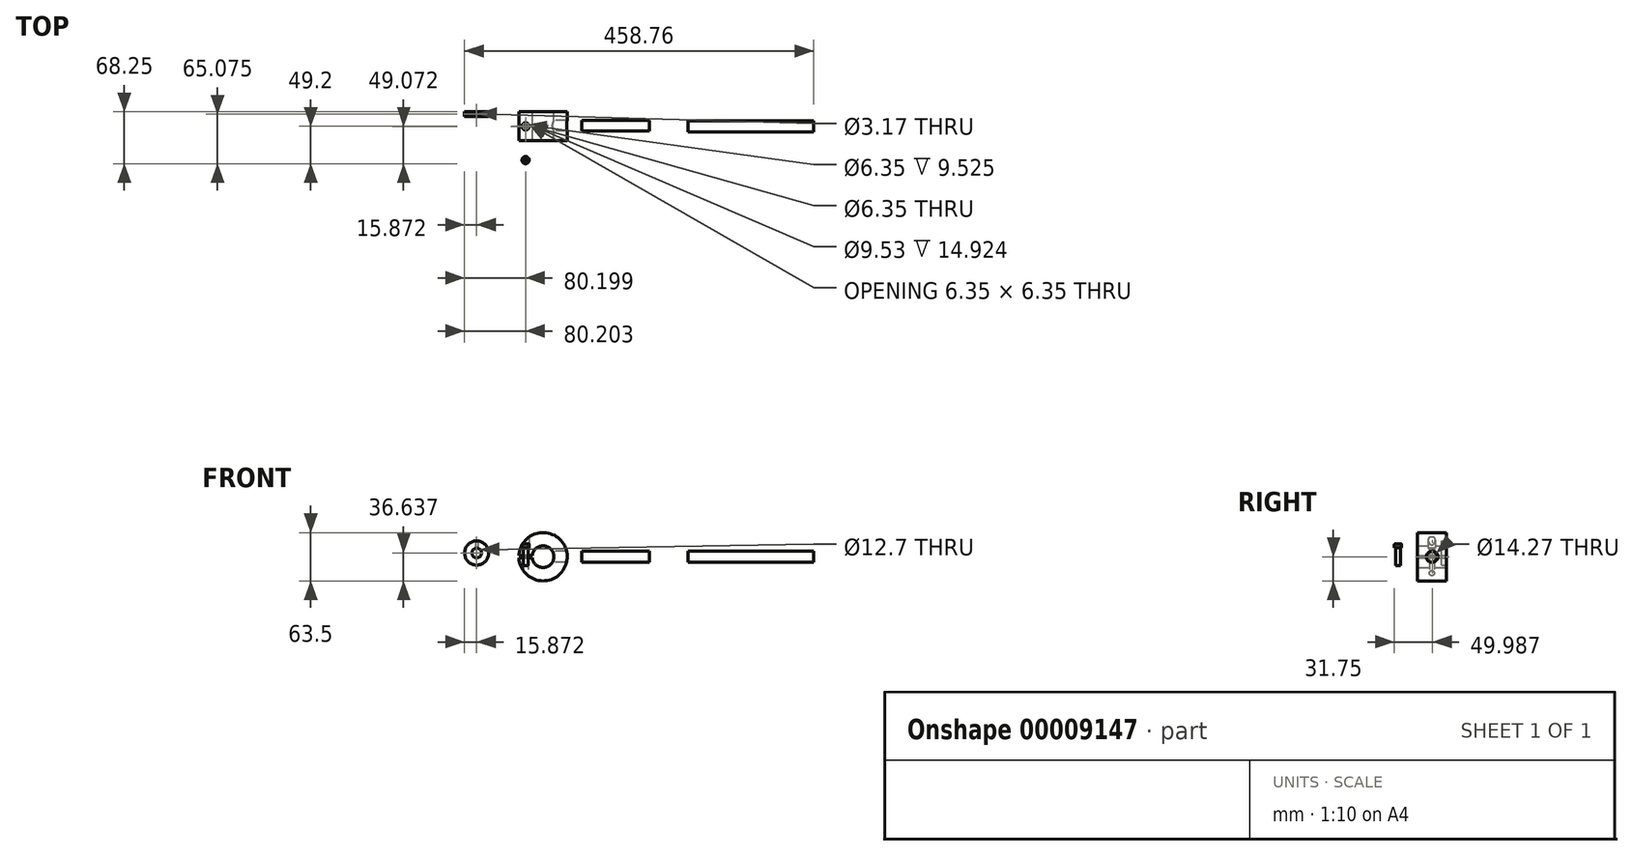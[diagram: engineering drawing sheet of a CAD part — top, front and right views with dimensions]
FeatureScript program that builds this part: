
annotation { "Feature Type Name" : "Feature", "Feature Type Description" : "" }
export const myFeature = defineFeature(function(context is Context, id is Id, definition is map)
    precondition{}
    {
        {
            var Q0;
            Q0=qCreatedBy(makeId("Front.planeOp"),FACE);
            var sketch = newSketch(context, id + "F0", { "sketchPlane" : qUnion([Q0])});
            skCircle(sketch, "E0", {"center": v(0, 0) * mm, "radius": 14.29 * mm});
            skCircle(sketch, "E1", {"center": v(0, 0) * mm, "radius": 31.75 * mm});
            skLineSegment(sketch, "E2", {"start": v(-31.71, 1.57) * mm, "end": v(-10.18, 1.57) * mm});
            skLineSegment(sketch, "E3", {"start": v(-31.71, -1.57) * mm, "end": v(-9.23, -1.57) * mm});
            skSolve(sketch);
        }
        {
            var Q0;
            {var subQ1=sQuery(id+"F0.wireOp",EDGE,"E0");var subQ5=sQuery(id+"F0.wireOp",EDGE,"E2");var subQ6=makeQuery(id+"F0.imprint","INTERSECT",VERTEX,{"derivedFrom":[subQ1,subQ5]});Q0=makeQuery(id+"F0.imprint","IMPRINT",FACE,{"disambiguationData":[TD([[makeQuery(id+"F0.imprint","IMPRINT",EDGE,{"disambiguationData":[TD([[subQ6,1.0]])],"derivedFrom":subQ1}),-1.0]])]});}
            extrude(context, id + "F1", {"entities" : qUnion([Q0]), "depth" : 38.1 * mm});
        }
        {
            var Q0;
            Q0=qCreatedBy(makeId("Right.planeOp"),FACE);
            cPlane(context, id + "F2", {"entities" : qUnion([Q0]), "cplaneType" : CPlaneType.OFFSET, "offset" : 50.8 * mm, "width" : 152.4 * mm, "height" : 152.4 * mm});
        }
        {
            var Q0;
            Q0=qCreatedBy(makeId("Right.planeOp"),FACE);
            var sketch = newSketch(context, id + "F3", { "sketchPlane" : qUnion([Q0])});
            skCircle(sketch, "E4", {"center": v(-18.26, 0) * mm, "radius": 7.14 * mm});
            skSolve(sketch);
        }
        {
            var Q0;
            Q0=makeQuery(id+"F3.imprint","IMPRINT",FACE,{"disambiguationData":[TD([[makeQuery(id+"F3.imprint","IMPRINT",EDGE,{"derivedFrom":sQuery(id+"F3.wireOp",EDGE,"E4")}),1.0]])]});
            extrude(context, id + "F4", {"entities" : qUnion([Q0]), "operationType" : NewBodyOperationType.REMOVE, "endBound" : BoundingType.THROUGH_ALL, "depth" : 25.4 * mm});
        }
        {
            var Q0;
            Q0=qCreatedBy(id+"F2.planeOp",FACE);
            var sketch = newSketch(context, id + "F5", { "sketchPlane" : qUnion([Q0])});
            skCircle(sketch, "E5", {"center": v(-18.26, 0) * mm, "radius": 7.14 * mm});
            skSolve(sketch);
        }
        {
            var Q0;
            Q0=makeQuery(id+"F5.imprint","IMPRINT",FACE,{"disambiguationData":[TD([[makeQuery(id+"F5.imprint","IMPRINT",EDGE,{"derivedFrom":sQuery(id+"F5.wireOp",EDGE,"E5")}),1.0]])]});
            extrude(context, id + "F6", {"entities" : qUnion([Q0]), "depth" : 88.9 * mm});
        }
        {
            var Q0;
            Q0=makeQuery(id+"F1.opExtrude","SWEPT_FACE",FACE,{"disambiguationData":[OSD([sQuery(id+"F0.wireOp",EDGE,"E3")])]});
            var sketch = newSketch(context, id + "F7", { "sketchPlane" : qUnion([Q0])});
            skLineSegment(sketch, "E6.bottom", {"start": v(-31.71, 0) * mm, "end": v(-14.25, 0) * mm});
            skLineSegment(sketch, "E6.top", {"start": v(-31.71, -38.1) * mm, "end": v(-14.25, -38.1) * mm});
            skLineSegment(sketch, "E6.left", {"start": v(-31.71, 0) * mm, "end": v(-31.71, -38.1) * mm});
            skLineSegment(sketch, "E6.right", {"start": v(-14.25, 0) * mm, "end": v(-14.25, -38.1) * mm});
            skCircle(sketch, "E7", {"center": v(-22.96, -19.05) * mm, "radius": 3.18 * mm});
            skSolve(sketch);
        }
        {
            var Q0;
            Q0=makeQuery(id+"F7.imprint","IMPRINT",FACE,{"disambiguationData":[TD([[makeQuery(id+"F7.imprint","IMPRINT",EDGE,{"derivedFrom":sQuery(id+"F7.wireOp",EDGE,"E7")}),1.0]])]});
            extrude(context, id + "F8", {"entities" : qUnion([Q0]), "operationType" : NewBodyOperationType.REMOVE, "endBound" : BoundingType.THROUGH_ALL, "depth" : 25.4 * mm, "hasSecondDirection" : true, "secondDirectionBound" : SecondDirectionBoundingType.THROUGH_ALL, "secondDirectionOppositeDirection" : true, "secondDirectionDepth" : 25.4 * mm});
        }
        {
            var Q0;
            Q0=makeQuery(id+"F1.opExtrude","SWEPT_FACE",FACE,{"disambiguationData":[OSD([sQuery(id+"F0.wireOp",EDGE,"E2")])]});
            cPlane(context, id + "F9", {"entities" : qUnion([Q0]), "cplaneType" : CPlaneType.OFFSET, "offset" : 12.7 * mm, "oppositeDirection" : true, "width" : 152.4 * mm, "height" : 152.4 * mm});
        }
        {
            var Q0;
            Q0=qCreatedBy(id+"F9.planeOp",FACE);
            var sketch = newSketch(context, id + "F10", { "sketchPlane" : qUnion([Q0])});
            skCircle(sketch, "E8", {"center": v(-22.96, 19.18) * mm, "radius": 4.76 * mm});
            skSolve(sketch);
        }
        {
            var Q0;
            Q0=makeQuery(id+"F10.imprint","IMPRINT",FACE,{"disambiguationData":[TD([[makeQuery(id+"F10.imprint","IMPRINT",EDGE,{"derivedFrom":sQuery(id+"F10.wireOp",EDGE,"E8")}),1.0]])]});
            extrude(context, id + "F11", {"entities" : qUnion([Q0]), "operationType" : NewBodyOperationType.REMOVE, "endBound" : BoundingType.THROUGH_ALL, "oppositeDirection" : true, "depth" : 25.4 * mm, "hasSecondDirection" : true, "secondDirectionOppositeDirection" : false, "secondDirectionDepth" : 3.17 * mm});
        }
        {
            var Q0;
            Q0=makeQuery(id+"F6.opExtrude","CAP_FACE",FACE,{"disambiguationData":[OSD([sQuery(id+"F5.wireOp",EDGE,"E5")])],"isStart":false});
            cPlane(context, id + "F12", {"entities" : qUnion([Q0]), "cplaneType" : CPlaneType.OFFSET, "offset" : 50.8 * mm, "width" : 152.4 * mm, "height" : 152.4 * mm});
        }
        {
            var Q0;
            Q0=qCreatedBy(id+"F12.planeOp",FACE);
            var sketch = newSketch(context, id + "F13", { "sketchPlane" : qUnion([Q0])});
            skCircle(sketch, "E9", {"center": v(-19.18, -0.1) * mm, "radius": 7.14 * mm});
            skSolve(sketch);
        }
        {
            var Q0;
            Q0=makeQuery(id+"F13.imprint","IMPRINT",FACE,{"disambiguationData":[TD([[makeQuery(id+"F13.imprint","IMPRINT",EDGE,{"derivedFrom":sQuery(id+"F13.wireOp",EDGE,"E9")}),1.0]])]});
            extrude(context, id + "F14", {"entities" : qUnion([Q0]), "depth" : 165.1 * mm});
        }
        {
            var Q0;
            Q0=makeQuery(id+"F1.opExtrude","CAP_FACE",FACE,{"disambiguationData":[OSD([sQuery(id+"F0.wireOp",EDGE,"E0"),sQuery(id+"F0.wireOp",EDGE,"E1"),sQuery(id+"F0.wireOp",EDGE,"E2"),sQuery(id+"F0.wireOp",EDGE,"E3")])],"isStart":false});
            cPlane(context, id + "F15", {"entities" : qUnion([Q0]), "cplaneType" : CPlaneType.OFFSET, "offset" : 25.4 * mm, "width" : 152.4 * mm, "height" : 152.4 * mm});
        }
        {
            var Q0;
            Q0=qCreatedBy(id+"F15.planeOp",FACE);
            var sketch = newSketch(context, id + "F16", { "sketchPlane" : qUnion([Q0])});
            skLineSegment(sketch, "E10", {"start": v(-23, 16.6) * mm, "end": v(-18.25, 16.6) * mm});
            skLineSegment(sketch, "E11", {"start": v(-18.25, 16.6) * mm, "end": v(-18.25, 11.84) * mm});
            skLineSegment(sketch, "E12", {"start": v(-18.25, 11.84) * mm, "end": v(-19.83, 11.84) * mm});
            skLineSegment(sketch, "E13", {"start": v(-19.83, 11.84) * mm, "end": v(-19.83, -11.98) * mm});
            skLineSegment(sketch, "E14", {"start": v(-19.83, -11.98) * mm, "end": v(-23, -11.98) * mm});
            skLineSegment(sketch, "E15", {"start": v(-23, -11.98) * mm, "end": v(-23, 16.6) * mm});
            skSolve(sketch);
        }
        {
            var Q0;
            Q0=makeQuery(id+"F16.imprint","IMPRINT",FACE,{"disambiguationData":[TD([[makeQuery(id+"F16.imprint","IMPRINT",EDGE,{"derivedFrom":sQuery(id+"F16.wireOp",EDGE,"E10")}),-1.0]])]});
            var Q1;
            Q1=sQuery(id+"F16.wireOp",EDGE,"E15");
            revolve(context, id + "F17", {"entities" : qUnion([Q0]), "axis" : qUnion([Q1]), "revolveType" : RevolveType.FULL});
        }
        {
            var Q0;
            Q0=makeQuery(id+"F17.opRevolve","SWEPT_FACE",FACE,{"disambiguationData":[OSD([sQuery(id+"F16.wireOp",EDGE,"E10")])]});
            var sketch = newSketch(context, id + "F18", { "sketchPlane" : qUnion([Q0])});
            skCircle(sketch, "E16.cCircle", {"center": v(-23, -63.5) * mm, "radius": 2.37 * mm, "construction": true});
            skLineSegment(sketch, "E16.0", {"start": v(-24.37, -61.13) * mm, "end": v(-21.63, -61.13) * mm});
            skLineSegment(sketch, "E16.1", {"start": v(-21.63, -61.13) * mm, "end": v(-20.26, -63.5) * mm});
            skLineSegment(sketch, "E16.2", {"start": v(-20.26, -63.5) * mm, "end": v(-21.63, -65.87) * mm});
            skLineSegment(sketch, "E16.3", {"start": v(-21.63, -65.87) * mm, "end": v(-24.37, -65.87) * mm});
            skLineSegment(sketch, "E16.4", {"start": v(-24.37, -65.87) * mm, "end": v(-25.75, -63.5) * mm});
            skLineSegment(sketch, "E16.5", {"start": v(-25.75, -63.5) * mm, "end": v(-24.37, -61.13) * mm});
            skPoint(sketch, "E16.0.midPoint", {"position": v(-23, -61.13) * mm});
            skSolve(sketch);
        }
        {
            var Q0;
            Q0=makeQuery(id+"F18.imprint","IMPRINT",FACE,{"disambiguationData":[TD([[makeQuery(id+"F18.imprint","IMPRINT",EDGE,{"derivedFrom":sQuery(id+"F18.wireOp",EDGE,"E16.0")}),-1.0]])]});
            extrude(context, id + "F19", {"entities" : qUnion([Q0]), "operationType" : NewBodyOperationType.REMOVE, "oppositeDirection" : true, "depth" : 4.75 * mm});
        }
        {
            var Q0;
            Q0=makeQuery(id+"F17.opRevolve","SWEPT_EDGE",EDGE,{"disambiguationData":[OSD([sQuery(id+"F16.wireOp",EDGE,"E10"),sQuery(id+"F16.wireOp",EDGE,"E11")])]});
            fillet(context, id + "F20", {"entities" : qUnion([Q0]), "radius" : 0.5 * mm, "tangentPropagation" : true, "allowEdgeOverflow" : false});
        }
        {
            var Q0;
            Q0=qCreatedBy(makeId("Front.planeOp"),FACE);
            var sketch = newSketch(context, id + "F21", { "sketchPlane" : qUnion([Q0])});
            skCircle(sketch, "E17", {"center": v(-87.29, 4.89) * mm, "radius": 15.88 * mm});
            skCircle(sketch, "E18", {"center": v(-87.29, 4.89) * mm, "radius": 6.35 * mm});
            skSolve(sketch);
        }
        {
            var Q0;
            Q0=makeQuery(id+"F21.imprint","IMPRINT",FACE,{"disambiguationData":[TD([[makeQuery(id+"F21.imprint","IMPRINT",EDGE,{"derivedFrom":sQuery(id+"F21.wireOp",EDGE,"E17")}),1.0]])]});
            extrude(context, id + "F22", {"entities" : qUnion([Q0]), "depth" : 6.35 * mm});
        }
        {
            var Q0;
            Q0=makeQuery(id+"F22.opExtrude","CAP_EDGE",EDGE,{"disambiguationData":[OSD([sQuery(id+"F21.wireOp",EDGE,"E17")])],"isStart":false});
            cPlane(context, id + "F23", {"entities" : qUnion([Q0]), "cplaneType" : CPlaneType.LINE_ANGLE, "offset" : 152.4 * mm, "angle" : 180 * degree, "width" : 152.4 * mm, "height" : 152.4 * mm});
        }
        {
            var Q0;
            Q0=qCreatedBy(id+"F23.planeOp",FACE);
            var sketch = newSketch(context, id + "F24", { "sketchPlane" : qUnion([Q0])});
            skLineSegment(sketch, "E19", {"start": v(-71.41, 0) * mm, "end": v(-71.41, -6.35) * mm});
            skLineSegment(sketch, "E20", {"start": v(-103.16, -6.35) * mm, "end": v(-103.16, 0) * mm});
            skLineSegment(sketch, "E21", {"start": v(-103.16, -3.18) * mm, "end": v(-71.41, -3.18) * mm, "construction": true});
            skCircle(sketch, "E22", {"center": v(-87.29, -3.18) * mm, "radius": 1.59 * mm});
            skSolve(sketch);
        }
        {
            var Q0;
            Q0=makeQuery(id+"F24.imprint","IMPRINT",FACE,{"disambiguationData":[TD([[makeQuery(id+"F24.imprint","IMPRINT",EDGE,{"derivedFrom":sQuery(id+"F24.wireOp",EDGE,"E22")}),1.0]])]});
            extrude(context, id + "F25", {"entities" : qUnion([Q0]), "operationType" : NewBodyOperationType.REMOVE, "endBound" : BoundingType.THROUGH_ALL, "depth" : 25.4 * mm});
        }
    });
